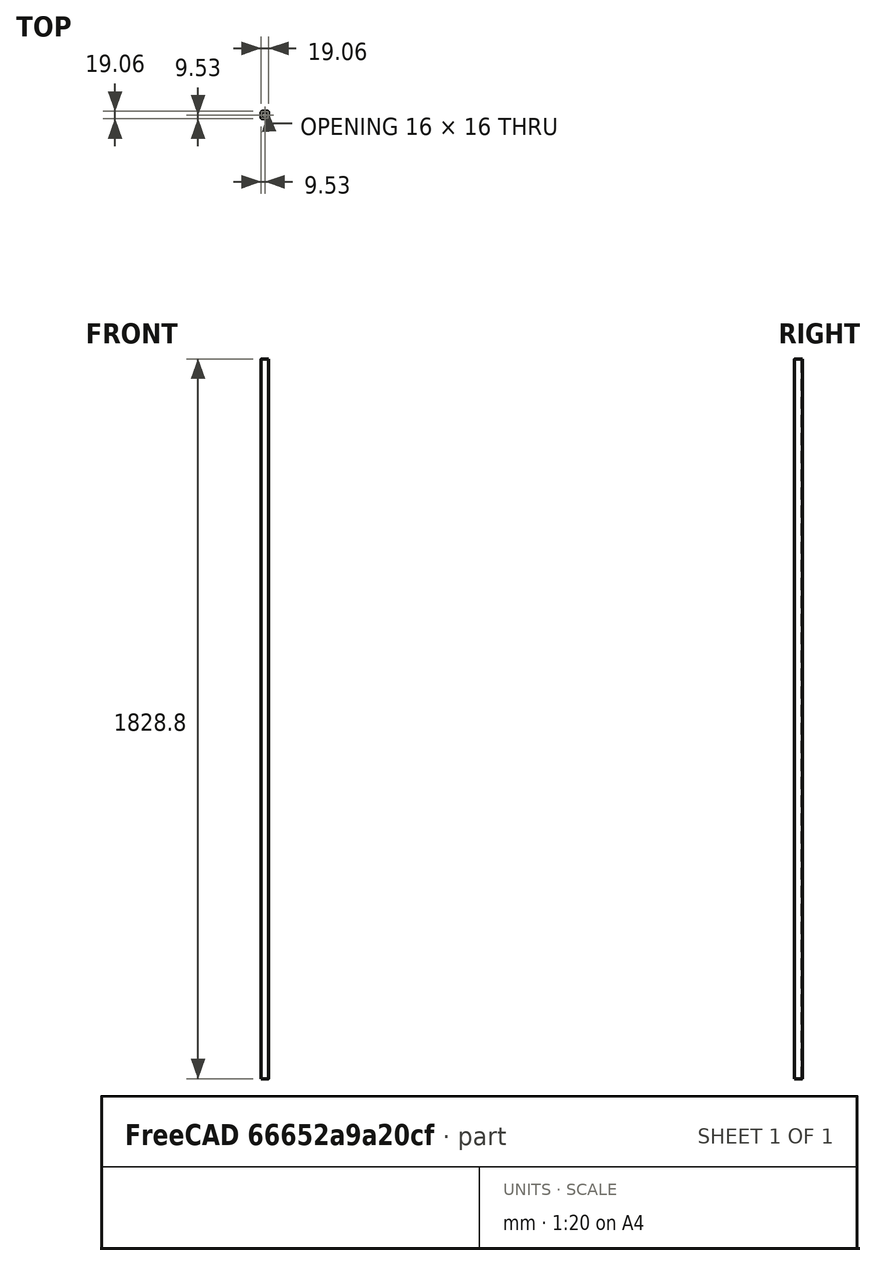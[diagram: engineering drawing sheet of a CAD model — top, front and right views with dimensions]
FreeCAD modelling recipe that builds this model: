
FCSTD DOCUMENT  (FreeCAD 0.20R29410 (Git))
Label: 6ftx.75squaretube
License: All rights reserved
LicenseURL: http://en.wikipedia.org/wiki/All_rights_reserved
objects: Sketcher::SketchObject×1, PartDesign::Pad×1, PartDesign::Body×1, Spreadsheet::Sheet×1
note: 4 computed .brp shape members not serialized (recipe doc carries the construction recipe); baked Part::Feature solids carry a one-line shape summary decoded from their .brp

FEATURE [Sketcher::SketchObject] Sketch002  label="3/4 tube"
  FullyConstrained = true
  MapMode = 5
  Support = -> [XY_Plane002]
  expr: Constraints[23] = Spreadsheet.wall
  expr: Constraints[28] = Spreadsheet.radius
  expr: Constraints[29] = Spreadsheet.radius
  expr: Constraints[30] = Spreadsheet.B2
  expr: Constraints[31] = Spreadsheet.B2
  sketch-geometry (16):
    g0: LineSegment StartX=-6.477 StartY=9.525 StartZ=0 EndX=6.477 EndY=9.525 EndZ=0
    g1: LineSegment StartX=9.525 StartY=6.477 StartZ=0 EndX=9.525 EndY=-6.477 EndZ=0
    g2: LineSegment StartX=6.477 StartY=-9.525 StartZ=0 EndX=-6.477 EndY=-9.525 EndZ=0
    g3: LineSegment StartX=-9.525 StartY=-6.477 StartZ=0 EndX=-9.525 EndY=6.477 EndZ=0
    g4: ArcOfCircle CenterX=-6.477 CenterY=6.477 CenterZ=0 NormalX=0 NormalY=0 NormalZ=1 AngleXU=0 Radius=3.048 StartAngle=1.5708 EndAngle=3.14159
    g5: ArcOfCircle CenterX=6.477 CenterY=6.477 CenterZ=0 NormalX=0 NormalY=0 NormalZ=1 AngleXU=0 Radius=3.048 StartAngle=0 EndAngle=1.5708
    g6: ArcOfCircle CenterX=6.477 CenterY=-6.477 CenterZ=0 NormalX=0 NormalY=0 NormalZ=1 AngleXU=0 Radius=3.048 StartAngle=4.71239 EndAngle=6.28319
    g7: ArcOfCircle CenterX=-6.477 CenterY=-6.477 CenterZ=0 NormalX=0 NormalY=0 NormalZ=1 AngleXU=0 Radius=3.048 StartAngle=3.14159 EndAngle=4.71239
    g8: LineSegment StartX=-6.477 StartY=8.001 StartZ=0 EndX=6.477 EndY=8.001 EndZ=0
    g9: LineSegment StartX=8.001 StartY=6.477 StartZ=0 EndX=8.001 EndY=-6.477 EndZ=0
    g10: LineSegment StartX=6.477 StartY=-8.001 StartZ=0 EndX=-6.477 EndY=-8.001 EndZ=0
    g11: LineSegment StartX=-8.001 StartY=-6.477 StartZ=0 EndX=-8.001 EndY=6.477 EndZ=0
    g12: ArcOfCircle CenterX=-6.477 CenterY=6.477 CenterZ=0 NormalX=0 NormalY=0 NormalZ=1 AngleXU=0 Radius=1.524 StartAngle=1.5708 EndAngle=3.14159
    g13: ArcOfCircle CenterX=6.477 CenterY=6.477 CenterZ=0 NormalX=0 NormalY=0 NormalZ=1 AngleXU=0 Radius=1.524 StartAngle=1e-16 EndAngle=1.5708
    g14: ArcOfCircle CenterX=6.477 CenterY=-6.477 CenterZ=0 NormalX=0 NormalY=0 NormalZ=1 AngleXU=0 Radius=1.524 StartAngle=4.71239 EndAngle=6.28319
    g15: ArcOfCircle CenterX=-6.477 CenterY=-6.477 CenterZ=0 NormalX=0 NormalY=0 NormalZ=1 AngleXU=0 Radius=1.524 StartAngle=3.14159 EndAngle=4.71239
  constraints (34):
    c: Horizontal(g0)
    c: Horizontal(g2)
    c: Vertical(g1)
    c: Vertical(g3)
    c: Tangent(g3,g4) = 1.5708
    c: Tangent(g0,g4) = 1.5708
    c: Tangent(g0,g5) = 1.5708
    c: Tangent(g1,g5) = 1.5708
    c: Tangent(g1,g6) = 1.5708
    c: Tangent(g2,g6) = 1.5708
    c: Tangent(g2,g7) = 1.5708
    c: Tangent(g3,g7) = 1.5708
    c: Horizontal(g8)
    c: Horizontal(g10)
    c: Vertical(g9)
    c: Tangent(g11,g12) = 1.5708
    c: Tangent(g8,g12) = 1.5708
    c: Tangent(g8,g13) = 1.5708
    c: Tangent(g9,g13) = 1.5708
    c: Tangent(g9,g14) = 1.5708
    c: Tangent(g10,g14) = 1.5708
    c: Tangent(g10,g15) = 1.5708
    c: Tangent(g11,g15) = 1.5708
    c: Distance(g11,g3) = 1.524
    c: Coincident(g6,g14)
    c: Coincident(g4,g12)
    c: Coincident(g5,g13)
    c: Coincident(g7,g15)
    c: Radius(g7) = 3.048
    c: Radius(g6) = 3.048
    c: Distance(g0,g2) = 19.05
    c: Distance(g3,g1) = 19.05
    c: Symmetric(g3,g1,g-2)
    c: Symmetric(g0,g2,g-1)
FEATURE [PartDesign::Pad] Pad
  Direction = (0,0,1)
  Length = 1828.8
  Length2 = 99.9998
  Profile = -> Sketch002
  Refine = true
  Type = 0
  expr: Length = Spreadsheet.Length
FEATURE [PartDesign::Body] Body002
  Group = -> [Sketch002,Pad]
  Origin = -> Origin002
  Tip = -> Pad
FEATURE [Spreadsheet::Sheet] Spreadsheet
  cells = A1=Description; B1=Value; A2=OD; B2==0.75in; A3=Wall Thickness; B3(wall)==0.06in; A4=Calculated Corner Radius; B4(radius)==2 * B3; A5=Length; B5(Length)==6ft
